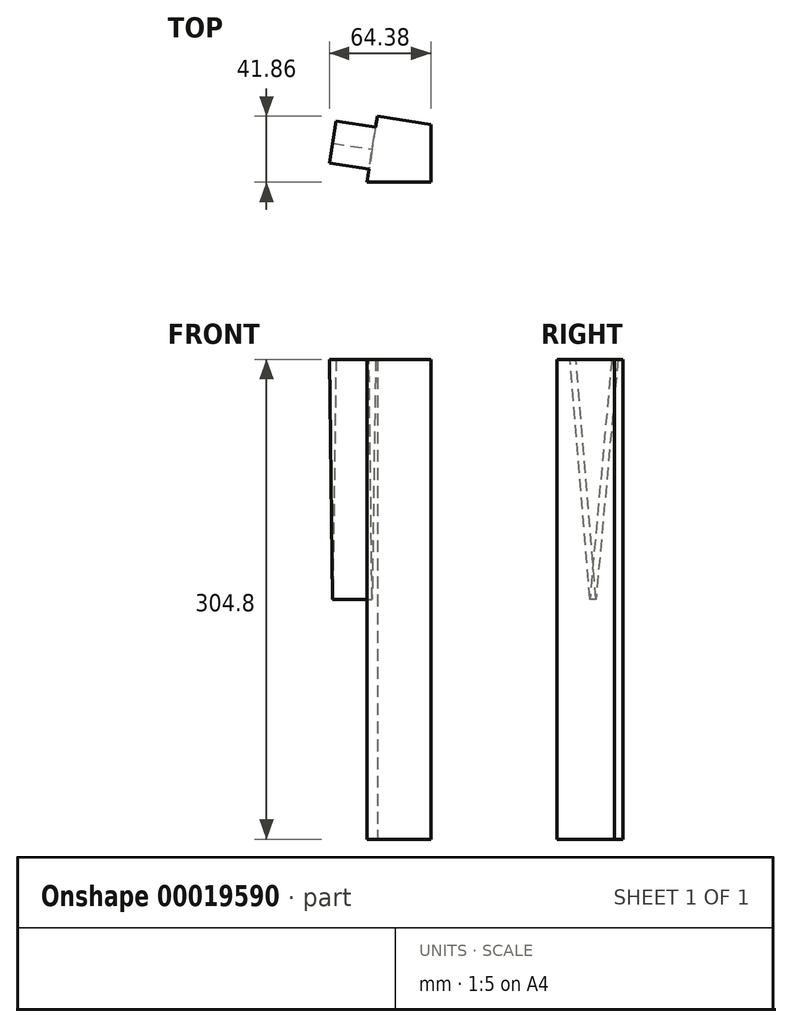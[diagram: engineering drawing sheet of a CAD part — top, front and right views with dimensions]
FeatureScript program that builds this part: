
annotation { "Feature Type Name" : "Feature", "Feature Type Description" : "" }
export const myFeature = defineFeature(function(context is Context, id is Id, definition is map)
    precondition{}
    {
        {
            var Q0;
            Q0=qCreatedBy(makeId("Top.planeOp"),FACE);
            var sketch = newSketch(context, id + "F0", { "sketchPlane" : qUnion([Q0])});
            skLineSegment(sketch, "E0", {"start": v(0, 0) * mm, "end": v(6.53, 41.86) * mm});
            skLineSegment(sketch, "E1", {"start": v(6.53, 41.86) * mm, "end": v(40.57, 36.55) * mm});
            skLineSegment(sketch, "E2", {"start": v(40.57, 36.55) * mm, "end": v(40.57, 0) * mm});
            skLineSegment(sketch, "E3", {"start": v(40.57, 0) * mm, "end": v(0, 0) * mm});
            skSolve(sketch);
        }
        {
            var Q0;
            Q0 = qSketchRegion(id + "F0", true);
            extrude(context, id + "F1", {"entities" : qUnion([Q0]), "depth" : 304.8 * mm});
        }
        {
            var Q0;
            Q0=makeQuery(id+"F1.opExtrude","SWEPT_FACE",FACE,{"disambiguationData":[OSD([sQuery(id+"F0.wireOp",EDGE,"E0")])]});
            var sketch = newSketch(context, id + "F2", { "sketchPlane" : qUnion([Q0])});
            skLineSegment(sketch, "E4", {"start": v(0, 152.4) * mm, "end": v(-21.18, 152.4) * mm});
            skLineSegment(sketch, "E5", {"start": v(-21.18, 152.4) * mm, "end": v(-42.37, 152.4) * mm});
            skLineSegment(sketch, "E6", {"start": v(-21.18, 152.4) * mm, "end": v(-8.33, 304.8) * mm});
            skLineSegment(sketch, "E7", {"start": v(-8.33, 304.8) * mm, "end": v(-35.3, 304.8) * mm});
            skLineSegment(sketch, "E8", {"start": v(-35.3, 304.8) * mm, "end": v(-21.18, 152.4) * mm});
            skSolve(sketch);
        }
        {
            var Q0;
            Q0=makeQuery(id+"F2.imprint","IMPRINT",FACE,{"disambiguationData":[TD([[makeQuery(id+"F2.imprint","IMPRINT",EDGE,{"derivedFrom":sQuery(id+"F2.wireOp",EDGE,"E6")}),1.0]])]});
            extrude(context, id + "F3", {"entities" : qUnion([Q0]), "operationType" : NewBodyOperationType.ADD, "depth" : 25.4 * mm});
        }
    });
